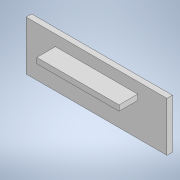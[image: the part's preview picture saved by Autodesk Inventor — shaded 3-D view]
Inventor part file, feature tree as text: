
AUTODESK INVENTOR PART (.ipt)
format: ipt  version: 2022 (Build 260153000, 153)  size: 102,912 bytes
history: native  units: mm
features: extrude x2, sketch x2
ambient origin geometry x8: Origin, YZ Plane, XZ Plane, XY Plane, X Axis, Y Axis, Z Axis, Center Point
bodies: Solid1 (feature_tree)
feature tree (4):
  extrude  "Extrusion1"  Depth=45.0mm
  extrude  "Extrusion2"  Depth=75.0mm
  sketch  "Sketch1"  dims[d0=128.37mm d1=45.0mm]
  sketch  "Sketch2"  dims[d2=5.0mm d3=0.0mm d4=75.0mm d5=5.0mm d6=10.0mm d7=17.0mm d8=0.0mm]
